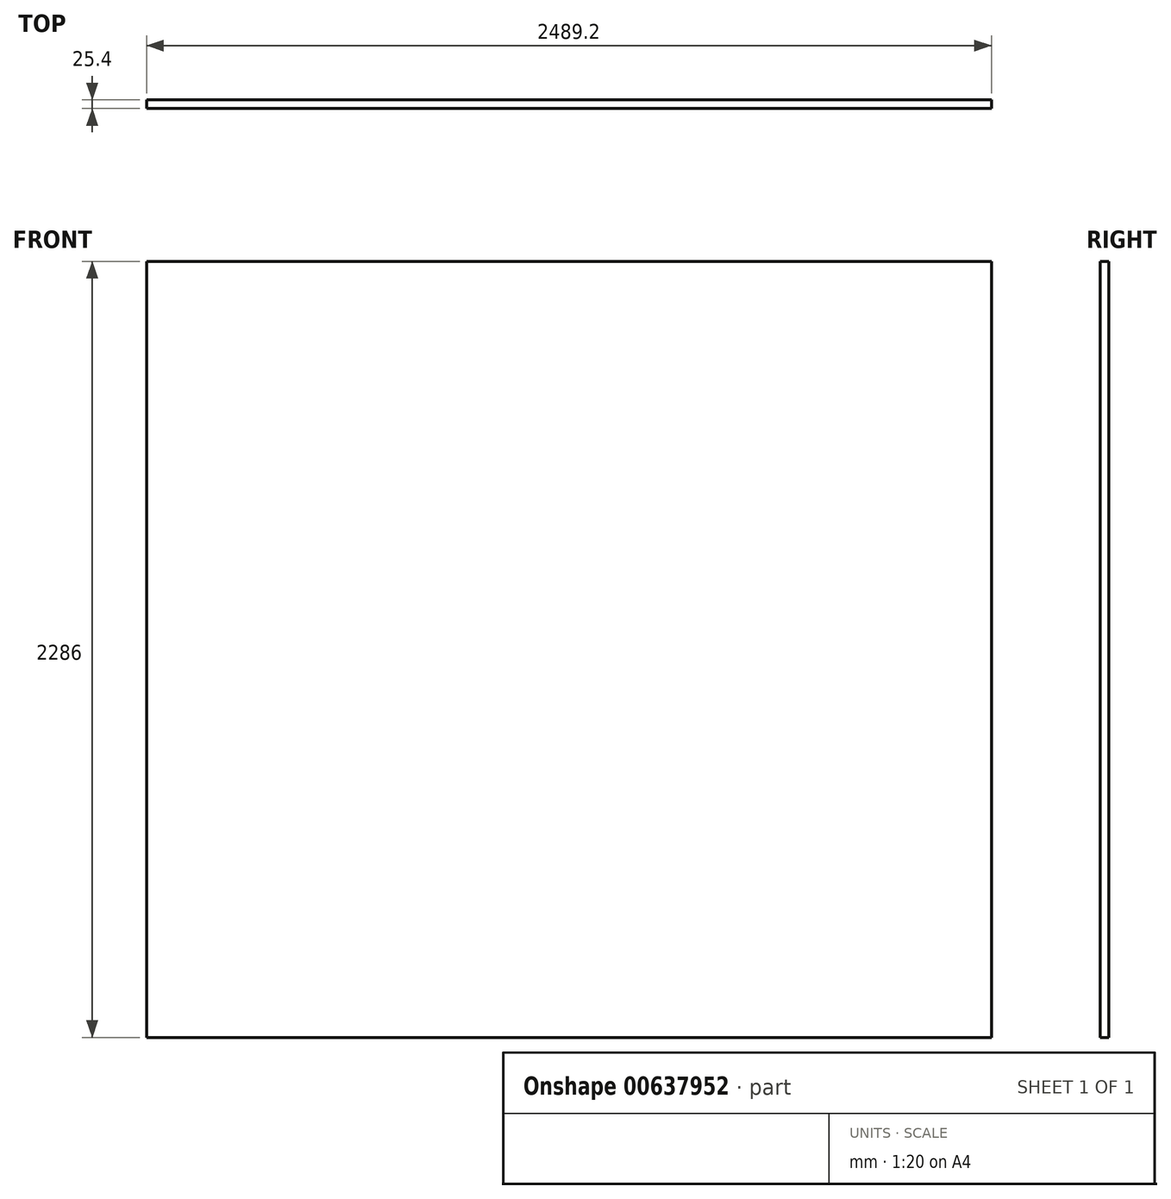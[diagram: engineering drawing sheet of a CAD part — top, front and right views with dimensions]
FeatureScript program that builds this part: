
annotation { "Feature Type Name" : "Feature", "Feature Type Description" : "" }
export const myFeature = defineFeature(function(context is Context, id is Id, definition is map)
    precondition{}
    {
        {
            var Q0;
            Q0=qCreatedBy(makeId("Front.planeOp"),FACE);
            var sketch = newSketch(context, id + "F0", { "sketchPlane" : qUnion([Q0])});
            skLineSegment(sketch, "E0.bottom", {"start": v(1244.6, 1143) * mm, "end": v(-1244.6, 1143) * mm});
            skLineSegment(sketch, "E0.top", {"start": v(1244.6, -1143) * mm, "end": v(-1244.6, -1143) * mm});
            skLineSegment(sketch, "E0.left", {"start": v(1244.6, 1143) * mm, "end": v(1244.6, -1143) * mm});
            skLineSegment(sketch, "E0.right", {"start": v(-1244.6, 1143) * mm, "end": v(-1244.6, -1143) * mm});
            skPoint(sketch, "E0.middle", {"position": v(0, 0) * mm});
            skSolve(sketch);
        }
        {
            var Q0;
            Q0 = qSketchRegion(id + "F0", true);
            extrude(context, id + "F1", {"entities" : qUnion([Q0]), "depth" : 25.4 * mm, "offsetDistance" : 25.4 * mm});
        }
    });
